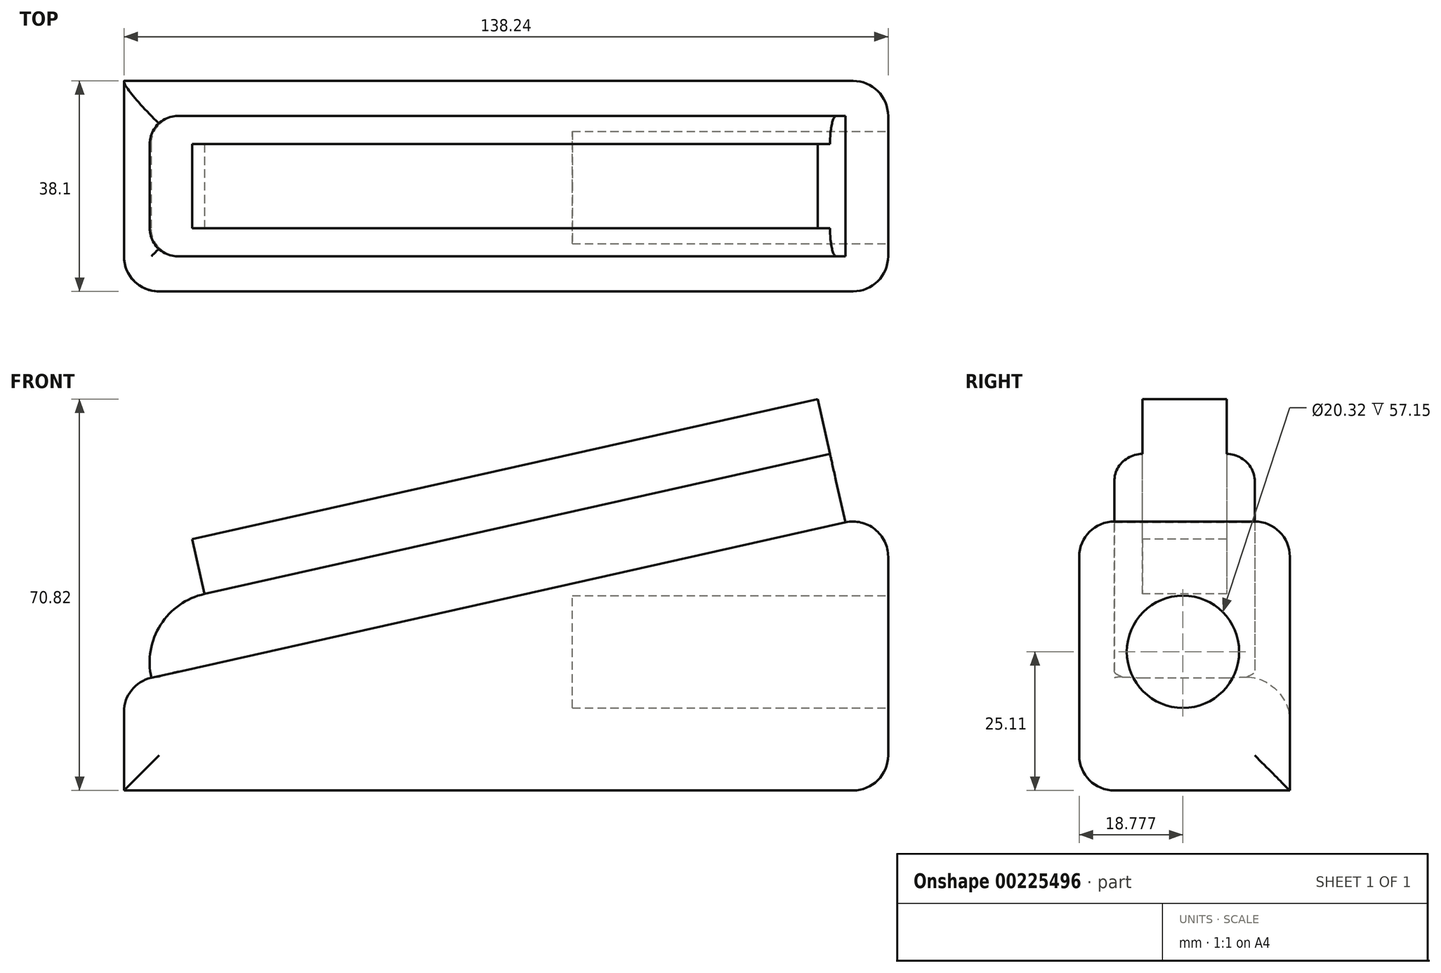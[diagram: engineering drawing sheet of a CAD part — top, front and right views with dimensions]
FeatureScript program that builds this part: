
annotation { "Feature Type Name" : "Feature", "Feature Type Description" : "" }
export const myFeature = defineFeature(function(context is Context, id is Id, definition is map)
    precondition{}
    {
        {
            var Q0;
            Q0=qCreatedBy(makeId("Front.planeOp"),FACE);
            var sketch = newSketch(context, id + "F0", { "sketchPlane" : qUnion([Q0])});
            skLineSegment(sketch, "E0", {"start": v(0, 0) * mm, "end": v(76.25, 0) * mm});
            skLineSegment(sketch, "E1", {"start": v(76.25, 0) * mm, "end": v(76.25, 50.25) * mm});
            skLineSegment(sketch, "E2", {"start": v(76.25, 50.25) * mm, "end": v(-61.99, 19.3) * mm});
            skLineSegment(sketch, "E3", {"start": v(-61.99, 19.3) * mm, "end": v(-61.99, 0) * mm});
            skLineSegment(sketch, "E4", {"start": v(-61.99, 0) * mm, "end": v(0, 0) * mm});
            skSolve(sketch);
        }
        {
            var Q0;
            Q0=makeQuery(id+"F0.imprint","IMPRINT",FACE,{"disambiguationData":[TD([[makeQuery(id+"F0.imprint","IMPRINT",EDGE,{"derivedFrom":sQuery(id+"F0.wireOp",EDGE,"E0")}),1.0]])]});
            extrude(context, id + "F1", {"entities" : qUnion([Q0]), "depth" : 38.1 * mm});
        }
        {
            var Q0;
            Q0=makeQuery(id+"F1.opExtrude","CAP_FACE",FACE,{"disambiguationData":[OSD([sQuery(id+"F0.wireOp",EDGE,"E0"),sQuery(id+"F0.wireOp",EDGE,"E1"),sQuery(id+"F0.wireOp",EDGE,"E2"),sQuery(id+"F0.wireOp",EDGE,"E3"),sQuery(id+"F0.wireOp",EDGE,"E4")])],"isStart":false});
            var Q1;
            Q1=makeQuery(id+"F1.opExtrude","CAP_EDGE",EDGE,{"disambiguationData":[OSD([sQuery(id+"F0.wireOp",EDGE,"E2")])],"isStart":true});
            var Q2;
            Q2=makeQuery(id+"F1.opExtrude","SWEPT_FACE",FACE,{"disambiguationData":[OSD([sQuery(id+"F0.wireOp",EDGE,"E1")])]});
            var Q3;
            Q3=makeQuery(id+"F1.opExtrude","SWEPT_EDGE",EDGE,{"disambiguationData":[OSD([sQuery(id+"F0.wireOp",EDGE,"E2"),sQuery(id+"F0.wireOp",EDGE,"E3")])]});
            fillet(context, id + "F2", {"entities" : qUnion([Q0, Q1, Q2, Q3]), "radius" : 6.35 * mm, "tangentPropagation" : true, "allowEdgeOverflow" : false});
        }
        {
            var Q0;
            Q0=makeQuery(id+"F1.opExtrude","SWEPT_FACE",FACE,{"disambiguationData":[OSD([sQuery(id+"F0.wireOp",EDGE,"E1")])]});
            var sketch = newSketch(context, id + "F3", { "sketchPlane" : qUnion([Q0])});
            skCircle(sketch, "E5", {"center": v(-19.32, 25.1) * mm, "radius": 10.16 * mm});
            skSolve(sketch);
        }
        {
            var Q0;
            Q0=makeQuery(id+"F3.imprint","IMPRINT",FACE,{"disambiguationData":[TD([[makeQuery(id+"F3.imprint","IMPRINT",EDGE,{"derivedFrom":sQuery(id+"F3.wireOp",EDGE,"E5")}),1.0]])]});
            extrude(context, id + "F4", {"entities" : qUnion([Q0]), "operationType" : NewBodyOperationType.REMOVE, "oppositeDirection" : true, "depth" : 57.15 * mm});
        }
        {
            var Q0;
            Q0=makeQuery(id+"F1.opExtrude","SWEPT_FACE",FACE,{"disambiguationData":[OSD([sQuery(id+"F0.wireOp",EDGE,"E2")])]});
            extrude(context, id + "F5", {"entities" : qUnion([Q0]), "operationType" : NewBodyOperationType.ADD, "depth" : 12.7 * mm});
        }
        {
            var Q0;
            Q0=makeQuery(id+"F5.opExtrude","CAP_EDGE",EDGE,{"disambiguationData":[OSD([sQuery(id+"F0.wireOp",EDGE,"E2"),sQuery(id+"F0.wireOp",EDGE,"E3")])],"isStart":false});
            fillet(context, id + "F6", {"entities" : qUnion([Q0]), "radius" : 12.7 * mm, "tangentPropagation" : true, "allowEdgeOverflow" : false});
        }
        {
            var Q0;
            {var subQ0=sQuery(id+"F0.wireOp",EDGE,"E2");Q0=makeQuery(id+"F5.opExtrude","CAP_EDGE",EDGE,{"disambiguationData":[OSD([subQ0]),TDD([makeQuery(id+"F2.opFillet","BLEND_EDGE",EDGE,{"blendedFrom":[makeQuery(id+"F1.opExtrude","CAP_EDGE",EDGE,{"disambiguationData":[OSD([subQ0])],"isStart":false}),makeQuery(id+"F1.opExtrude","SWEPT_FACE",FACE,{"disambiguationData":[OSD([subQ0])]})],"blendedInto":[makeQuery(id+"F1.opExtrude","SWEPT_FACE",FACE,{"disambiguationData":[OSD([subQ0])]})]})])],"isStart":false});}
            fillet(context, id + "F7", {"entities" : qUnion([Q0]), "radius" : 5.08 * mm, "tangentPropagation" : true, "allowEdgeOverflow" : false});
        }
        {
            var Q0;
            {var subQ0=sQuery(id+"F0.wireOp",EDGE,"E2");Q0=makeQuery(id+"F5.opExtrude","CAP_EDGE",EDGE,{"disambiguationData":[OSD([subQ0]),TDD([makeQuery(id+"F2.opFillet","BLEND_EDGE",EDGE,{"blendedFrom":[makeQuery(id+"F1.opExtrude","CAP_EDGE",EDGE,{"disambiguationData":[OSD([subQ0])],"isStart":true}),makeQuery(id+"F1.opExtrude","SWEPT_FACE",FACE,{"disambiguationData":[OSD([subQ0])]})],"blendedInto":[makeQuery(id+"F1.opExtrude","SWEPT_FACE",FACE,{"disambiguationData":[OSD([subQ0])]})]})])],"isStart":false});}
            fillet(context, id + "F8", {"entities" : qUnion([Q0]), "radius" : 5.08 * mm, "tangentPropagation" : true, "allowEdgeOverflow" : false});
        }
        {
            var Q0;
            Q0=makeQuery(id+"F5.opExtrude","CAP_FACE",FACE,{"disambiguationData":[OSD([sQuery(id+"F0.wireOp",EDGE,"E2")])],"isStart":false});
            extrude(context, id + "F9", {"entities" : qUnion([Q0]), "operationType" : NewBodyOperationType.ADD, "depth" : 10.16 * mm});
        }
    });
